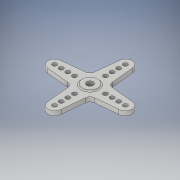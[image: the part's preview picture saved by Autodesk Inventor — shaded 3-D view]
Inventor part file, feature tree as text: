
AUTODESK INVENTOR PART (.ipt)
format: ipt  version: 2019 (Build 230136000, 136)  size: 224,768 bytes
history: native  units: mm
features: extrude x4, sketch x4, fillet x2, mirror x1, pattern_circular x1
ambient origin geometry x8: Origin, YZ Plane, XZ Plane, XY Plane, X Axis, Y Axis, Z Axis, Center Point
bodies: Solide1 (feature_tree)
feature tree (12):
  extrude  "Extrusion1"  Depth=38.0mm
  mirror  "Symétrie1"
  pattern_circular  "Réseau circulaire1"  [2 undecoded]
  extrude  "Extrusion2"  TaperAngle=135.0deg  [1 undecoded]
  fillet  "Congé1"  Radius=2.0mm
  extrude  "Extrusion3"  Depth=7.0mm
  fillet  "Congé2"  Radius=2.0mm
  extrude  "Extrusion4"  Depth=10.0mm
  sketch  "Esquisse1"
  sketch  "Esquisse2"
  sketch  "Esquisse3"
  sketch  "Esquisse4"
note: 3 required parameter values undecoded (feature->parameter linkage not recoverable at this tier; creation-order binding heuristic only, values carry confidence <= 0.55)
